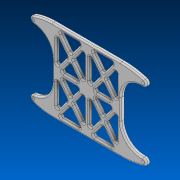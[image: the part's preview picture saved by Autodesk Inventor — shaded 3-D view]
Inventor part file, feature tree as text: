
AUTODESK INVENTOR PART (.ipt)
format: ipt  version: 2022 (Build 260153000, 153)  size: 538,112 bytes
history: native  units: in
note: dims shown in document units (in); Inventor stores cm internally (conversion verified against a paired STEP export)
features: fillet x4, sketch x3, extrude x2, hole x2, mirror x1, projected_geometry x1
ambient origin geometry x8: Origin, YZ Plane, XZ Plane, XY Plane, X Axis, Y Axis, Z Axis, Center Point
bodies: Solid1 (feature_tree)
feature tree (13):
  sketch  "Sketch1"  dims[d0=5.0in d1=6.0in d2=0.25in d3=0.0in]
  extrude  "Extrusion1"  Depth=6.0in
  fillet  "Fillet1"  Radius=0.25in
  hole  "Hole2"  [1 undecoded]
  fillet  "Fillet4"  Radius=0.15in
  extrude  "Extrusion2"  Depth=0.15in
  fillet  "Fillet2"  Radius=0.15in
  fillet  "Fillet3"  Radius=0.15in
  hole  "Hole1"  [1 undecoded]
  mirror  "Mirror1"
  sketch  "Sketch2"  dims[d4=0.25in d5=0.15in d6=0.15in]
  projected_geometry  "Projected Loop1"
  sketch  "Sketch3"  dims[d7=0.15in d8=0.15in d9=0.15in d10=0.15in d11=0.125in d12=1.0in d13=2.3125in d14=0.125in d15=7.0in d16=0.125in d17=0.125in d18=1.0in d19=0.0in d20=0.15in d21=0.05in d22=0.5in d23=0.18in d24=0.75in d25=0.375in d26=0.25in d27=0.5635in d28=1.0in d29=0.8108in d30=0.5in d31=0.175in d32=0.75in d33=0.35in d34=0.2in d35=0.5635in d36=1.0in d37=0.8108in d38=5.0in d39=2.5in d40=0.1in d41=8.0in d42=1.5in]
note: 2 required parameter values undecoded (feature->parameter linkage not recoverable at this tier; creation-order binding heuristic only, values carry confidence <= 0.55)
